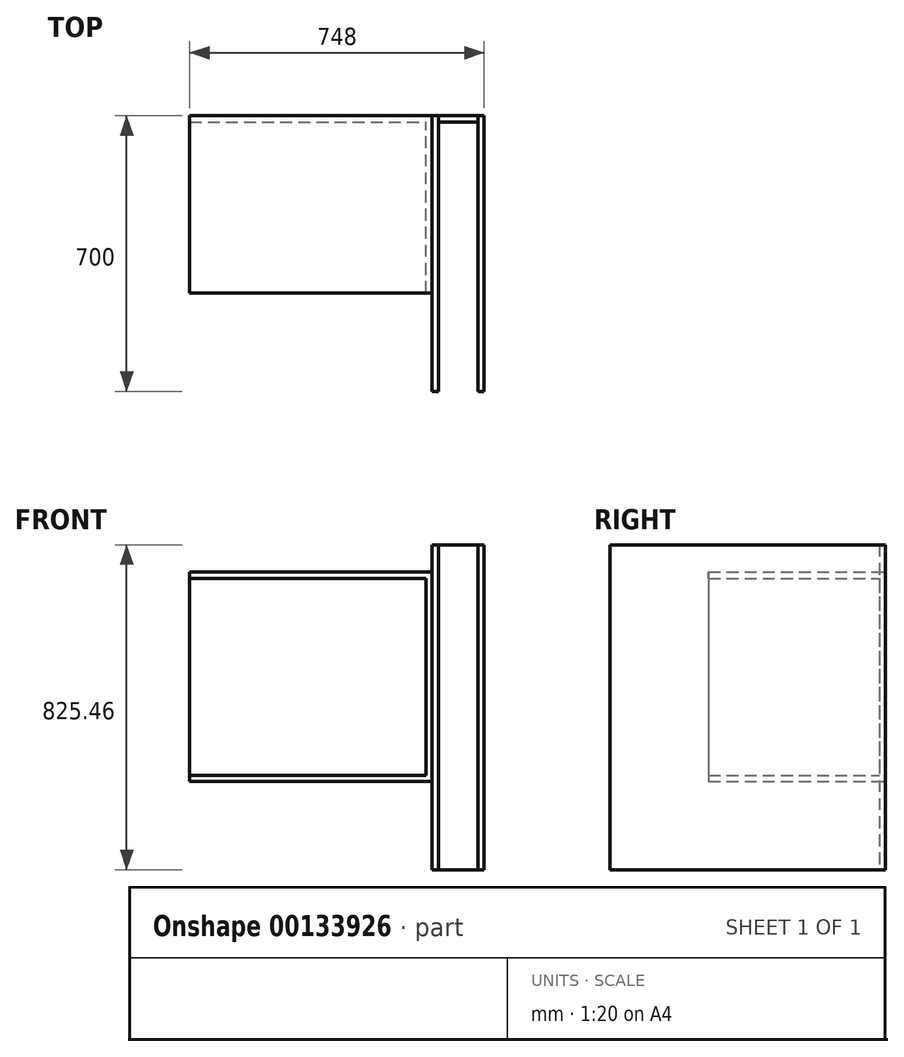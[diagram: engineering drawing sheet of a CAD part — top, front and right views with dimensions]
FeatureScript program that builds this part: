
annotation { "Feature Type Name" : "Feature", "Feature Type Description" : "" }
export const myFeature = defineFeature(function(context is Context, id is Id, definition is map)
    precondition{}
    {
        {
            var Q0;
            Q0=qCreatedBy(makeId("Front.planeOp"),FACE);
            var sketch = newSketch(context, id + "F0", { "sketchPlane" : qUnion([Q0])});
            skLineSegment(sketch, "E0.bottom", {"start": v(0, 0) * mm, "end": v(-500, 0) * mm, "construction": true});
            skLineSegment(sketch, "E0.top", {"start": v(0, 500) * mm, "end": v(-500, 500) * mm, "construction": true});
            skLineSegment(sketch, "E0.left", {"start": v(0, 0) * mm, "end": v(0, 500) * mm, "construction": true});
            skLineSegment(sketch, "E0.right", {"start": v(-500, 0) * mm, "end": v(-500, 500) * mm, "construction": true});
            skLineSegment(sketch, "E1.bottom", {"start": v(-3103.46, 2279.42) * mm, "end": v(-2503.46, 2279.42) * mm});
            skLineSegment(sketch, "E1.top", {"start": v(-3103.46, 1779.42) * mm, "end": v(-2503.46, 1779.42) * mm});
            skLineSegment(sketch, "E1.left", {"start": v(-3103.46, 2279.42) * mm, "end": v(-3103.46, 1779.42) * mm});
            skLineSegment(sketch, "E1.right", {"start": v(-2503.46, 2279.42) * mm, "end": v(-2503.46, 1779.42) * mm});
            skLineSegment(sketch, "E2.0", {"start": v(-3119.46, 2295.42) * mm, "end": v(-2487.46, 2295.42) * mm});
            skLineSegment(sketch, "E2.1", {"start": v(-3119.46, 2295.42) * mm, "end": v(-3119.46, 1763.42) * mm});
            skLineSegment(sketch, "E2.2", {"start": v(-3119.46, 1763.42) * mm, "end": v(-2487.46, 1763.42) * mm});
            skLineSegment(sketch, "E2.3", {"start": v(-2487.46, 2295.42) * mm, "end": v(-2487.46, 1763.42) * mm});
            skLineSegment(sketch, "E3.bottom", {"start": v(-2487.46, 2364.93) * mm, "end": v(-2471.46, 2364.93) * mm});
            skLineSegment(sketch, "E3.top", {"start": v(-2487.46, 1539.47) * mm, "end": v(-2471.46, 1539.47) * mm});
            skLineSegment(sketch, "E3.left", {"start": v(-2487.46, 2364.93) * mm, "end": v(-2487.46, 1539.47) * mm});
            skLineSegment(sketch, "E3.right", {"start": v(-2471.46, 2364.93) * mm, "end": v(-2471.46, 1539.47) * mm});
            skLineSegment(sketch, "E4.bottom", {"start": v(-2371.46, 2364.93) * mm, "end": v(-2355.46, 2364.93) * mm});
            skLineSegment(sketch, "E4.top", {"start": v(-2371.46, 1539.47) * mm, "end": v(-2355.46, 1539.47) * mm});
            skLineSegment(sketch, "E4.left", {"start": v(-2371.46, 2364.93) * mm, "end": v(-2371.46, 1539.47) * mm});
            skLineSegment(sketch, "E4.right", {"start": v(-2355.46, 2364.93) * mm, "end": v(-2355.46, 1539.47) * mm});
            skLineSegment(sketch, "E5.bottom", {"start": v(-2471.46, 1539.47) * mm, "end": v(-2371.46, 1539.47) * mm});
            skLineSegment(sketch, "E5.top", {"start": v(-2471.46, 1539.47) * mm, "end": v(-2371.46, 1539.47) * mm});
            skLineSegment(sketch, "E5.left", {"start": v(-2471.46, 1539.47) * mm, "end": v(-2471.46, 1539.47) * mm});
            skLineSegment(sketch, "E5.right", {"start": v(-2371.46, 1539.47) * mm, "end": v(-2371.46, 1539.47) * mm});
            skLineSegment(sketch, "E6", {"start": v(-2471.46, 2364.93) * mm, "end": v(-2371.46, 2364.93) * mm});
            skLineSegment(sketch, "E7", {"start": v(-3103.46, 2279.42) * mm, "end": v(-3103.46, 2295.42) * mm});
            skLineSegment(sketch, "E8", {"start": v(-3103.46, 1779.42) * mm, "end": v(-3103.46, 1763.42) * mm});
            skSolve(sketch);
        }
        {
            var Q0;
            Q0=makeQuery(id+"F0.imprint","IMPRINT",FACE,{"disambiguationData":[TD([[makeQuery(id+"F0.imprint","IMPRINT",EDGE,{"derivedFrom":sQuery(id+"F0.wireOp",EDGE,"E1.bottom")}),1.0]])]});
            extrude(context, id + "F1", {"entities" : qUnion([Q0]), "depth" : 450 * mm});
        }
        {
            var Q0;
            Q0=makeQuery(id+"F0.imprint","IMPRINT",FACE,{"disambiguationData":[TD([[makeQuery(id+"F0.imprint","IMPRINT",EDGE,{"derivedFrom":sQuery(id+"F0.wireOp",EDGE,"E1.bottom")}),-1.0]])]});
            extrude(context, id + "F2", {"entities" : qUnion([Q0]), "operationType" : NewBodyOperationType.ADD, "depth" : 16 * mm});
        }
        {
            var Q0;
            {var subQ2=sQuery(id+"F0.wireOp",EDGE,"E3.bottom");Q0=makeQuery(id+"F0.imprint","IMPRINT",FACE,{"disambiguationData":[TD([[makeQuery(id+"F0.imprint","IMPRINT",EDGE,{"derivedFrom":subQ2}),-1.0]])]});}
            var Q1;
            Q1=makeQuery(id+"F0.imprint","IMPRINT",FACE,{"disambiguationData":[TD([[makeQuery(id+"F0.imprint","IMPRINT",EDGE,{"derivedFrom":sQuery(id+"F0.wireOp",EDGE,"E4.bottom")}),-1.0]])]});
            extrude(context, id + "F3", {"entities" : qUnion([Q0, Q1]), "depth" : 700 * mm});
        }
        {
            var Q0;
            Q0=makeQuery(id+"F0.imprint","IMPRINT",FACE,{"disambiguationData":[TD([[makeQuery(id+"F0.imprint","IMPRINT",EDGE,{"derivedFrom":sQuery(id+"F0.wireOp",EDGE,"E3.right")}),1.0]])]});
            extrude(context, id + "F4", {"entities" : qUnion([Q0]), "depth" : 16 * mm});
        }
    });
